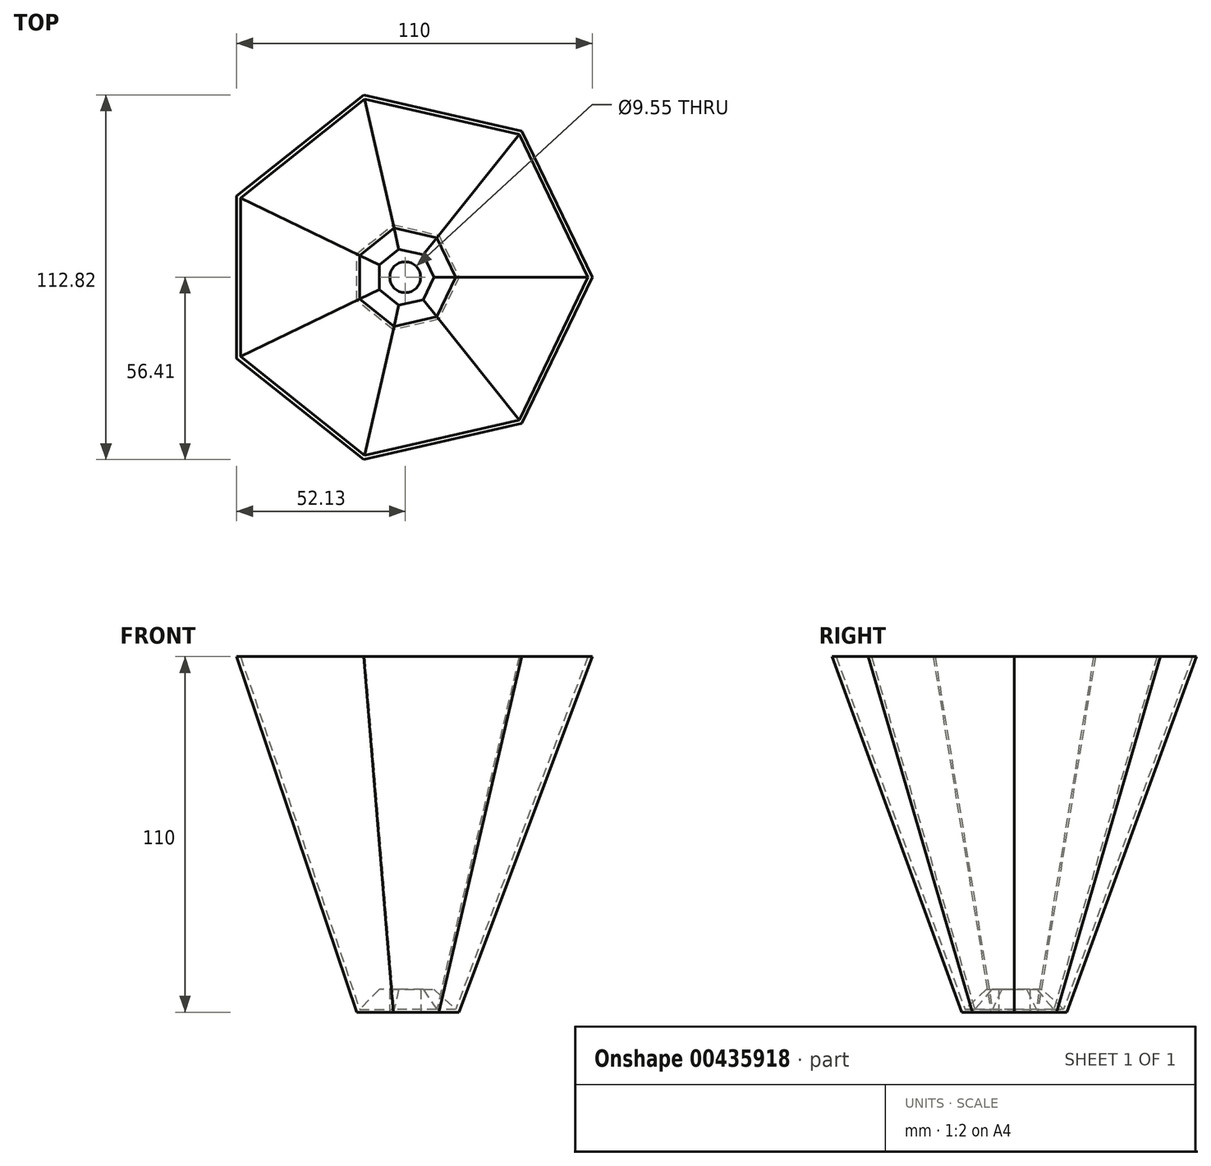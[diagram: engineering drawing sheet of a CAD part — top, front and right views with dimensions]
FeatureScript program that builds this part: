
annotation { "Feature Type Name" : "Feature", "Feature Type Description" : "" }
export const myFeature = defineFeature(function(context is Context, id is Id, definition is map)
    precondition{}
    {
        {
            var Q0;
            Q0=qCreatedBy(makeId("Top.planeOp"),FACE);
            var sketch = newSketch(context, id + "F0", { "sketchPlane" : qUnion([Q0])});
            skCircle(sketch, "E0.cCircle", {"center": v(0, 0) * mm, "radius": 15 * mm, "construction": true});
            skLineSegment(sketch, "E0.0", {"start": v(16.65, 0) * mm, "end": v(10.38, -13.02) * mm});
            skLineSegment(sketch, "E0.1", {"start": v(10.38, -13.02) * mm, "end": v(-3.7, -16.23) * mm});
            skLineSegment(sketch, "E0.2", {"start": v(-3.7, -16.23) * mm, "end": v(-15, -7.22) * mm});
            skLineSegment(sketch, "E0.3", {"start": v(-15, -7.22) * mm, "end": v(-15, 7.22) * mm});
            skLineSegment(sketch, "E0.4", {"start": v(-15, 7.22) * mm, "end": v(-3.7, 16.23) * mm});
            skLineSegment(sketch, "E0.5", {"start": v(-3.7, 16.23) * mm, "end": v(10.38, 13.02) * mm});
            skLineSegment(sketch, "E0.6", {"start": v(10.38, 13.02) * mm, "end": v(16.65, 0) * mm});
            skPoint(sketch, "E0.0.midPoint", {"position": v(13.51, -6.5) * mm});
            skSolve(sketch);
        }
        {
            var Q0;
            Q0 = qSketchRegion(id + "F0", true);
            extrude(context, id + "F1", {"entities" : qUnion([Q0]), "depth" : 7 * mm});
        }
        {
            var Q0;
            Q0=qCreatedBy(makeId("Top.planeOp"),FACE);
            cPlane(context, id + "F2", {"entities" : qUnion([Q0]), "cplaneType" : CPlaneType.OFFSET, "offset" : 110 * mm, "width" : 150 * mm, "height" : 150 * mm});
        }
        {
            var Q0;
            Q0=qCreatedBy(id+"F2.planeOp",FACE);
            var sketch = newSketch(context, id + "F3", { "sketchPlane" : qUnion([Q0])});
            skCircle(sketch, "E1.cCircle", {"center": v(0, 0) * mm, "radius": 52.13 * mm, "construction": true});
            skLineSegment(sketch, "E1.0", {"start": v(-12.88, -56.41) * mm, "end": v(-52.13, -25.1) * mm});
            skLineSegment(sketch, "E1.1", {"start": v(-52.13, -25.1) * mm, "end": v(-52.13, 25.1) * mm});
            skLineSegment(sketch, "E1.2", {"start": v(-52.13, 25.1) * mm, "end": v(-12.88, 56.41) * mm});
            skLineSegment(sketch, "E1.3", {"start": v(-12.88, 56.41) * mm, "end": v(36.08, 45.24) * mm});
            skLineSegment(sketch, "E1.4", {"start": v(36.08, 45.24) * mm, "end": v(57.87, 0) * mm});
            skLineSegment(sketch, "E1.5", {"start": v(57.87, 0) * mm, "end": v(36.08, -45.24) * mm});
            skLineSegment(sketch, "E1.6", {"start": v(36.08, -45.24) * mm, "end": v(-12.88, -56.41) * mm});
            skPoint(sketch, "E1.0.midPoint", {"position": v(-32.5, -40.76) * mm});
            skSolve(sketch);
        }
        {
            var Q0;
            Q0=makeQuery(id+"F1.opExtrude","CAP_FACE",FACE,{"disambiguationData":[OSD([sQuery(id+"F0.wireOp",EDGE,"E0.0"),sQuery(id+"F0.wireOp",EDGE,"E0.1"),sQuery(id+"F0.wireOp",EDGE,"E0.2"),sQuery(id+"F0.wireOp",EDGE,"E0.3"),sQuery(id+"F0.wireOp",EDGE,"E0.4"),sQuery(id+"F0.wireOp",EDGE,"E0.5"),sQuery(id+"F0.wireOp",EDGE,"E0.6")])],"isStart":true});
            var sketch = newSketch(context, id + "F4", { "sketchPlane" : qUnion([Q0])});
            skLineSegment(sketch, "E2.0", {"start": v(-13.8, 6.65) * mm, "end": v(-13.8, -6.65) * mm});
            skLineSegment(sketch, "E2.1", {"start": v(-3.4, 14.93) * mm, "end": v(-13.8, 6.65) * mm});
            skLineSegment(sketch, "E2.2", {"start": v(-3.4, -14.93) * mm, "end": v(9.55, -11.98) * mm});
            skLineSegment(sketch, "E2.3", {"start": v(9.55, -11.98) * mm, "end": v(15.32, 0) * mm});
            skLineSegment(sketch, "E2.4", {"start": v(15.32, 0) * mm, "end": v(9.55, 11.98) * mm});
            skLineSegment(sketch, "E2.5", {"start": v(-13.8, -6.65) * mm, "end": v(-3.4, -14.93) * mm});
            skLineSegment(sketch, "E2.6", {"start": v(9.55, 11.98) * mm, "end": v(-3.4, 14.93) * mm});
            skSolve(sketch);
        }
        {
            var Q0;
            Q0=makeQuery(id+"F3.imprint","IMPRINT",FACE,{"disambiguationData":[TD([[makeQuery(id+"F3.imprint","IMPRINT",EDGE,{"derivedFrom":sQuery(id+"F3.wireOp",EDGE,"E1.0")}),-1.0]])]});
            var sketch = newSketch(context, id + "F5", { "sketchPlane" : qUnion([Q0])});
            skLineSegment(sketch, "E3.0", {"start": v(-12.58, -55.12) * mm, "end": v(-50.93, -24.53) * mm});
            skLineSegment(sketch, "E3.1", {"start": v(35.25, -44.2) * mm, "end": v(-12.58, -55.12) * mm});
            skLineSegment(sketch, "E3.2", {"start": v(-50.93, 24.53) * mm, "end": v(-12.58, 55.12) * mm});
            skLineSegment(sketch, "E3.3", {"start": v(-12.58, 55.12) * mm, "end": v(35.25, 44.2) * mm});
            skLineSegment(sketch, "E3.4", {"start": v(35.25, 44.2) * mm, "end": v(56.53, 0) * mm});
            skLineSegment(sketch, "E3.5", {"start": v(-50.93, -24.53) * mm, "end": v(-50.93, 24.53) * mm});
            skLineSegment(sketch, "E3.6", {"start": v(56.53, 0) * mm, "end": v(35.25, -44.2) * mm});
            skSolve(sketch);
        }
        {
            var Q1;
            Q1 = qSketchRegion(id + "F3", true);
            var Q2;
            Q2=makeQuery(id+"F1.opExtrude","CAP_FACE",FACE,{"disambiguationData":[OSD([sQuery(id+"F0.wireOp",EDGE,"E0.0"),sQuery(id+"F0.wireOp",EDGE,"E0.1"),sQuery(id+"F0.wireOp",EDGE,"E0.2"),sQuery(id+"F0.wireOp",EDGE,"E0.3"),sQuery(id+"F0.wireOp",EDGE,"E0.4"),sQuery(id+"F0.wireOp",EDGE,"E0.5"),sQuery(id+"F0.wireOp",EDGE,"E0.6")])],"isStart":true});
            loft(context, id + "F6", {"operationType" : NewBodyOperationType.ADD, "sheetProfilesArray" : [{ "sheetProfileEntities" : qUnion([Q1]) }, { "sheetProfileEntities" : qUnion([Q2]) }]});
        }
        {
            var Q1;
            Q1=makeQuery(id+"F5.imprint","IMPRINT",FACE,{"disambiguationData":[TD([[makeQuery(id+"F5.imprint","IMPRINT",EDGE,{"derivedFrom":sQuery(id+"F5.wireOp",EDGE,"E3.0")}),-1.0]])]});
            var Q2;
            Q2=makeQuery(id+"F4.imprint","IMPRINT",FACE,{"disambiguationData":[TD([[makeQuery(id+"F4.imprint","IMPRINT",EDGE,{"derivedFrom":sQuery(id+"F4.wireOp",EDGE,"E2.0")}),1.0]])]});
            loft(context, id + "F7", {"operationType" : NewBodyOperationType.REMOVE, "sheetProfilesArray" : [{ "sheetProfileEntities" : qUnion([Q1]) }, { "sheetProfileEntities" : qUnion([Q2]) }]});
        }
        {
            var Q0;
            Q0=makeQuery(id+"F4.imprint","IMPRINT",FACE,{"disambiguationData":[TD([[makeQuery(id+"F4.imprint","IMPRINT",EDGE,{"derivedFrom":sQuery(id+"F4.wireOp",EDGE,"E2.0")}),1.0]])]});
            var Q1;
            Q1=makeQuery(id+"F4.imprint","IMPRINT",FACE,{"disambiguationData":[TD([[makeQuery(id+"F4.imprint","IMPRINT",EDGE,{"derivedFrom":sQuery(id+"F4.wireOp",EDGE,"E2.0")}),-1.0]])]});
            extrude(context, id + "F8", {"entities" : qUnion([Q0, Q1]), "operationType" : NewBodyOperationType.ADD, "oppositeDirection" : true, "depth" : 7 * mm});
        }
        {
            var Q0;
            Q0=makeQuery(id+"F4.imprint","IMPRINT",FACE,{"disambiguationData":[TD([[makeQuery(id+"F4.imprint","IMPRINT",EDGE,{"derivedFrom":sQuery(id+"F4.wireOp",EDGE,"E2.0")}),1.0]])]});
            var sketch = newSketch(context, id + "F9", { "sketchPlane" : qUnion([Q0])});
            skCircle(sketch, "E4", {"center": v(0, 0) * mm, "radius": 4.78 * mm});
            skSolve(sketch);
        }
        {
            var Q0;
            Q0=makeQuery(id+"F9.imprint","IMPRINT",FACE,{"disambiguationData":[TD([[makeQuery(id+"F9.imprint","IMPRINT",EDGE,{"derivedFrom":sQuery(id+"F9.wireOp",EDGE,"E4")}),1.0]])]});
            extrude(context, id + "F10", {"entities" : qUnion([Q0]), "operationType" : NewBodyOperationType.REMOVE, "oppositeDirection" : true, "depth" : 124.3 * mm});
        }
        {
            var Q0;
            Q0=makeQuery(id+"F8.opExtrude","CAP_EDGE",EDGE,{"disambiguationData":[OSD([sQuery(id+"F0.wireOp",EDGE,"E0.4")])],"isStart":false});
            var Q1;
            Q1=makeQuery(id+"F8.opExtrude","CAP_EDGE",EDGE,{"disambiguationData":[OSD([sQuery(id+"F0.wireOp",EDGE,"E0.3")])],"isStart":false});
            var Q2;
            Q2=makeQuery(id+"F8.opExtrude","CAP_EDGE",EDGE,{"disambiguationData":[OSD([sQuery(id+"F0.wireOp",EDGE,"E0.2")])],"isStart":false});
            var Q3;
            Q3=makeQuery(id+"F8.opExtrude","CAP_EDGE",EDGE,{"disambiguationData":[OSD([sQuery(id+"F0.wireOp",EDGE,"E0.1")])],"isStart":false});
            var Q4;
            Q4=makeQuery(id+"F8.opExtrude","CAP_EDGE",EDGE,{"disambiguationData":[OSD([sQuery(id+"F0.wireOp",EDGE,"E0.0")])],"isStart":false});
            var Q5;
            Q5=makeQuery(id+"F8.opExtrude","CAP_EDGE",EDGE,{"disambiguationData":[OSD([sQuery(id+"F0.wireOp",EDGE,"E0.6")])],"isStart":false});
            var Q6;
            Q6=makeQuery(id+"F8.opExtrude","CAP_EDGE",EDGE,{"disambiguationData":[OSD([sQuery(id+"F0.wireOp",EDGE,"E0.5")])],"isStart":false});
            chamfer(context, id + "F11", {"entities" : qUnion([Q0, Q1, Q2, Q3, Q4, Q5, Q6]), "width" : 7 * mm, "tangentPropagation" : true});
        }
    });
